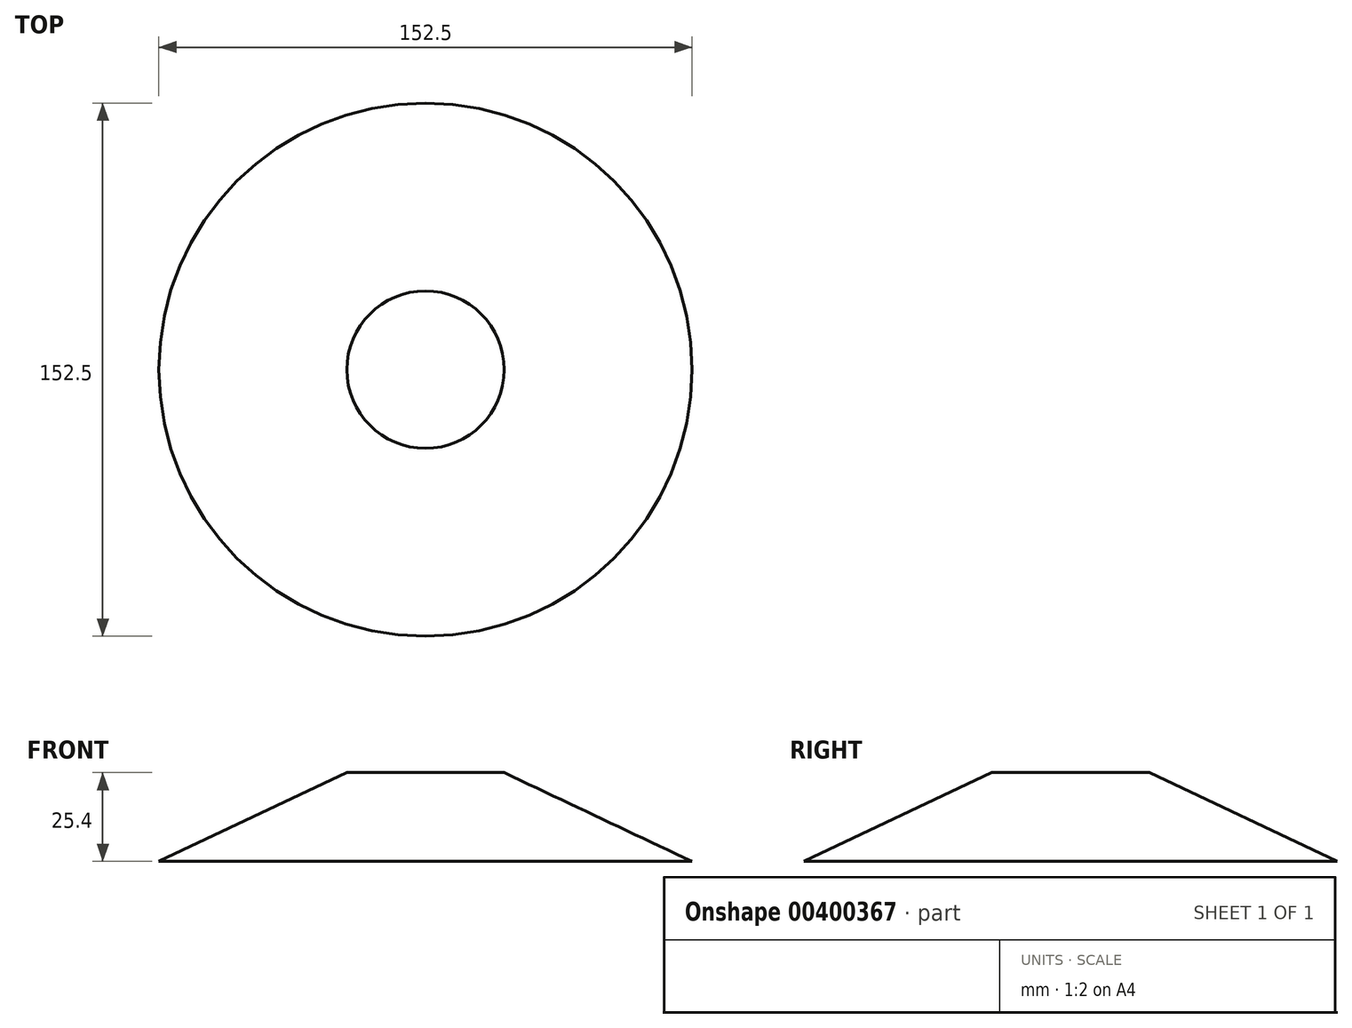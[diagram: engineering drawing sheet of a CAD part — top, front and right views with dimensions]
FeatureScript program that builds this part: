
annotation { "Feature Type Name" : "Feature", "Feature Type Description" : "" }
export const myFeature = defineFeature(function(context is Context, id is Id, definition is map)
    precondition{}
    {
        {
            var Q0;
            Q0=qCreatedBy(makeId("Top.planeOp"),FACE);
            cPlane(context, id + "F0", {"entities" : qUnion([Q0]), "cplaneType" : CPlaneType.OFFSET, "offset" : 25.4 * mm, "width" : 152.4 * mm, "height" : 152.4 * mm});
        }
        {
            var Q0;
            Q0=qCreatedBy(id+"F0.planeOp",FACE);
            var sketch = newSketch(context, id + "F1", { "sketchPlane" : qUnion([Q0])});
            skCircle(sketch, "E0", {"center": v(0, 0) * mm, "radius": 22.5 * mm});
            skSolve(sketch);
        }
        {
            var Q0;
            Q0=qCreatedBy(makeId("Top.planeOp"),FACE);
            var sketch = newSketch(context, id + "F2", { "sketchPlane" : qUnion([Q0])});
            skCircle(sketch, "E1", {"center": v(0, 0) * mm, "radius": 76.25 * mm});
            skSolve(sketch);
        }
        {
            var Q0;
            Q0 = qSketchRegion(id + "F1", true);
            var Q1;
            Q1 = qSketchRegion(id + "F2", true);
            loft(context, id + "F3", {"sheetProfilesArray" : [{ "sheetProfileEntities" : qUnion([Q0]) }, { "sheetProfileEntities" : qUnion([Q1]) }]});
        }
    });
